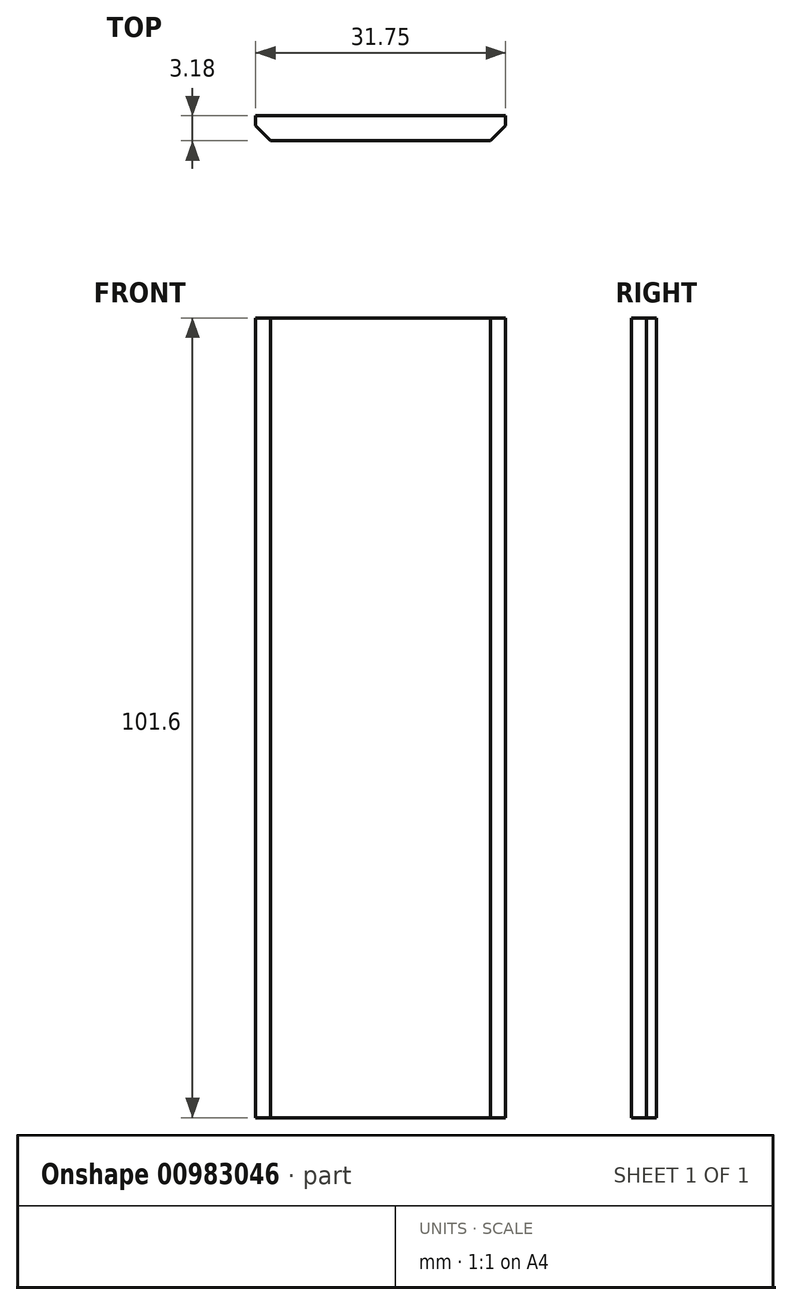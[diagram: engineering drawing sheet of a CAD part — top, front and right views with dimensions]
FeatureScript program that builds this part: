
annotation { "Feature Type Name" : "Feature", "Feature Type Description" : "" }
export const myFeature = defineFeature(function(context is Context, id is Id, definition is map)
    precondition{}
    {
        {
            var Q0;
            Q0=qCreatedBy(makeId("Front.planeOp"),FACE);
            var sketch = newSketch(context, id + "F0", { "sketchPlane" : qUnion([Q0])});
            skLineSegment(sketch, "E0.bottom", {"start": v(0, 0) * mm, "end": v(31.75, 0) * mm});
            skLineSegment(sketch, "E0.top", {"start": v(0, 101.6) * mm, "end": v(31.75, 101.6) * mm});
            skLineSegment(sketch, "E0.left", {"start": v(0, 0) * mm, "end": v(0, 101.6) * mm});
            skLineSegment(sketch, "E0.right", {"start": v(31.75, 0) * mm, "end": v(31.75, 101.6) * mm});
            skSolve(sketch);
        }
        {
            var Q0;
            Q0 = qSketchRegion(id + "F0", true);
            extrude(context, id + "F1", {"entities" : qUnion([Q0]), "depth" : 3.17 * mm, "offsetDistance" : 25.4 * mm});
        }
        {
            var Q0;
            Q0=makeQuery(id+"F1.opExtrude","CAP_EDGE",EDGE,{"disambiguationData":[OSD([sQuery(id+"F0.wireOp",EDGE,"E0.left")])],"isStart":false});
            var Q1;
            Q1=makeQuery(id+"F1.opExtrude","CAP_EDGE",EDGE,{"disambiguationData":[OSD([sQuery(id+"F0.wireOp",EDGE,"E0.right")])],"isStart":false});
            chamfer(context, id + "F2", {"entities" : qUnion([Q0, Q1]), "width" : 1.9 * mm, "tangentPropagation" : true});
        }
    });
